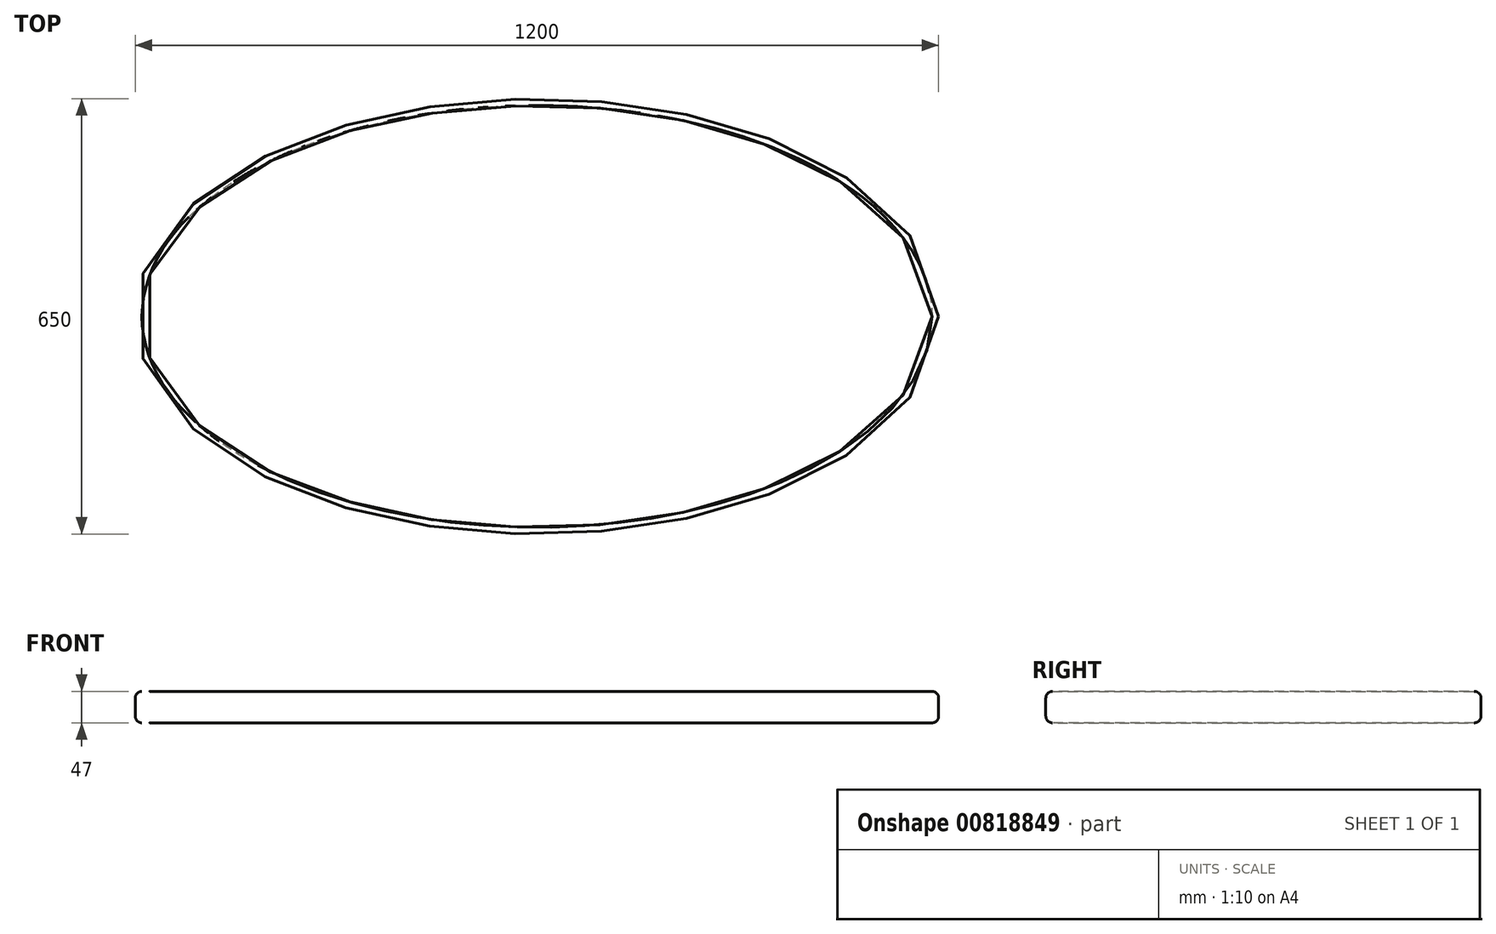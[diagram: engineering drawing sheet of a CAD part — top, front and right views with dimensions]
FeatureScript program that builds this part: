
annotation { "Feature Type Name" : "Feature", "Feature Type Description" : "" }
export const myFeature = defineFeature(function(context is Context, id is Id, definition is map)
    precondition{}
    {
        {
            var Q0;
            Q0=qCreatedBy(makeId("Top.planeOp"),FACE);
            var sketch = newSketch(context, id + "F0", { "sketchPlane" : qUnion([Q0])});
            skEllipse(sketch, "E0", {"center": v(0, 0) * mm, "majorRadius": 600 * mm, "minorRadius": 325 * mm, "majorAxis": v(1, 0)});
            skSolve(sketch);
        }
        {
            var Q0;
            Q0 = qSketchRegion(id + "F0", true);
            extrude(context, id + "F1", {"entities" : qUnion([Q0]), "depth" : 22 * mm, "offsetDistance" : 25 * mm});
        }
        {
            var Q0;
            Q0=makeQuery(id+"F1.opExtrude","CAP_FACE",FACE,{"disambiguationData":[OSD([sQuery(id+"F0.wireOp",EDGE,"E0")])],"isStart":true});
            var sketch = newSketch(context, id + "F2", { "sketchPlane" : qUnion([Q0])});
            skEllipse(sketch, "E1.0", {"center": v(0, 0) * mm, "majorRadius": 600 * mm, "minorRadius": 325 * mm, "majorAxis": v(1, 0)});
            skFitSpline(sketch, "E2.0", {"points": [v(577.9, -7.07) * mm, v(578.05, 0) * mm, v(577.9, 7.07) * mm, v(577.4, 14.11) * mm, v(576.6, 21.14) * mm, v(575.1, 30.5) * mm, v(572.43, 42.15) * mm, v(566.44, 60.74) * mm, v(555.74, 83.82) * mm, v(537.72, 111.12) * mm, v(518.37, 133.32) * mm, v(500.33, 150.6) * mm, v(485.53, 163.29) * mm, v(469.48, 175.66) * mm, v(455.07, 185.68) * mm, v(442.94, 193.5) * mm, v(433.54, 199.27) * mm, v(425.45, 203.99) * mm, v(418.83, 207.7) * mm, v(413.8, 210.47) * mm, v(408.7, 213.2) * mm, v(401.8, 216.8) * mm, v(393.06, 221.2) * mm, v(382.32, 226.33) * mm, v(367.72, 232.98) * mm, v(348.91, 240.9) * mm, v(325.53, 249.8) * mm, v(301.4, 258.07) * mm, v(268.25, 268.23) * mm, v(225.17, 279.26) * mm, v(180.22, 287.98) * mm, v(143.35, 293.52) * mm, v(115.3, 296.95) * mm, v(86.88, 299.64) * mm, v(62.95, 301.25) * mm, v(43.68, 302.15) * mm, v(29.17, 302.64) * mm, v(17.04, 302.89) * mm, v(7.3, 302.98) * mm, v(0, 303) * mm, v(-7.3, 302.98) * mm, v(-17.04, 302.89) * mm, v(-29.17, 302.64) * mm, v(-43.68, 302.15) * mm, v(-62.95, 301.25) * mm, v(-86.88, 299.64) * mm, v(-115.3, 296.95) * mm, v(-143.35, 293.52) * mm, v(-180.22, 287.98) * mm, v(-225.17, 279.26) * mm, v(-268.25, 268.23) * mm, v(-301.4, 258.07) * mm, v(-325.53, 249.8) * mm, v(-348.91, 240.9) * mm, v(-367.72, 232.98) * mm, v(-382.32, 226.33) * mm, v(-393.06, 221.2) * mm, v(-401.8, 216.8) * mm, v(-408.7, 213.2) * mm, v(-413.8, 210.47) * mm, v(-418.83, 207.7) * mm, v(-425.45, 203.99) * mm, v(-433.54, 199.27) * mm, v(-442.94, 193.5) * mm, v(-455.07, 185.68) * mm, v(-469.48, 175.66) * mm, v(-485.53, 163.29) * mm, v(-500.33, 150.6) * mm, v(-518.37, 133.32) * mm, v(-537.72, 111.12) * mm, v(-555.74, 83.82) * mm, v(-566.44, 60.74) * mm, v(-572.43, 42.15) * mm, v(-575.1, 30.5) * mm, v(-576.6, 21.14) * mm, v(-577.4, 14.11) * mm, v(-577.9, 7.07) * mm, v(-578.05, 0) * mm, v(-577.9, -7.07) * mm, v(-577.4, -14.11) * mm, v(-576.6, -21.14) * mm, v(-575.1, -30.5) * mm, v(-572.43, -42.15) * mm, v(-566.44, -60.74) * mm, v(-555.74, -83.82) * mm, v(-537.72, -111.12) * mm, v(-518.37, -133.32) * mm, v(-500.33, -150.6) * mm, v(-485.53, -163.29) * mm, v(-469.48, -175.66) * mm, v(-455.07, -185.68) * mm, v(-442.94, -193.5) * mm, v(-433.54, -199.27) * mm, v(-425.45, -203.99) * mm, v(-418.83, -207.7) * mm, v(-413.8, -210.47) * mm, v(-408.7, -213.2) * mm, v(-401.8, -216.8) * mm, v(-393.06, -221.2) * mm, v(-382.32, -226.33) * mm, v(-367.72, -232.98) * mm, v(-348.91, -240.9) * mm, v(-325.53, -249.8) * mm, v(-301.4, -258.07) * mm, v(-268.25, -268.23) * mm, v(-225.17, -279.26) * mm, v(-180.22, -287.98) * mm, v(-143.35, -293.52) * mm, v(-115.3, -296.95) * mm, v(-86.88, -299.64) * mm, v(-62.95, -301.25) * mm, v(-43.68, -302.15) * mm, v(-29.17, -302.64) * mm, v(-17.04, -302.89) * mm, v(-7.3, -302.98) * mm, v(0, -303) * mm, v(7.3, -302.98) * mm, v(17.04, -302.89) * mm, v(29.17, -302.64) * mm, v(43.68, -302.15) * mm, v(62.95, -301.25) * mm, v(86.88, -299.64) * mm, v(115.3, -296.95) * mm, v(143.35, -293.52) * mm, v(180.22, -287.98) * mm, v(225.17, -279.26) * mm, v(268.25, -268.23) * mm, v(301.4, -258.07) * mm, v(325.53, -249.8) * mm, v(348.91, -240.9) * mm, v(367.72, -232.98) * mm, v(382.32, -226.33) * mm, v(393.06, -221.2) * mm, v(401.8, -216.8) * mm, v(408.7, -213.2) * mm, v(413.8, -210.47) * mm, v(418.83, -207.7) * mm, v(425.45, -203.99) * mm, v(433.54, -199.27) * mm, v(442.94, -193.5) * mm, v(455.07, -185.68) * mm, v(469.48, -175.66) * mm, v(485.53, -163.29) * mm, v(500.33, -150.6) * mm, v(518.37, -133.32) * mm, v(537.72, -111.12) * mm, v(555.74, -83.82) * mm, v(566.44, -60.74) * mm, v(572.43, -42.15) * mm, v(575.1, -30.5) * mm, v(576.6, -21.14) * mm, v(577.4, -14.11) * mm, v(577.9, -7.07) * mm, v(578.05, 0) * mm, v(577.9, 7.07) * mm, v(577.9, -7.07) * mm]});
            skSolve(sketch);
        }
        {
            var Q0;
            Q0 = qSketchRegion(id + "F2", true);
            extrude(context, id + "F3", {"entities" : qUnion([Q0]), "operationType" : NewBodyOperationType.ADD, "depth" : 25 * mm, "offsetDistance" : 25 * mm});
        }
        {
            var Q0;
            Q0=makeQuery(id+"F3.boolean.opBoolean","MERGE",FACE,{"derivedFrom":[makeQuery(id+"F1.opExtrude","SWEPT_FACE",FACE,{"disambiguationData":[OSD([sQuery(id+"F0.wireOp",EDGE,"E0")])]}),makeQuery(id+"F3.opExtrude","SWEPT_FACE",FACE,{"disambiguationData":[OSD([sQuery(id+"F2.wireOp",EDGE,"E1.0")])]})]});
            fillet(context, id + "F4", {"entities" : qUnion([Q0]), "radius" : 10 * mm, "tangentPropagation" : true, "allowEdgeOverflow" : false});
        }
        {
            var Q0;
            Q0=makeQuery(id+"F0.imprint","IMPRINT",FACE,{"disambiguationData":[TD([[makeQuery(id+"F0.imprint","IMPRINT",EDGE,{"derivedFrom":sQuery(id+"F0.wireOp",EDGE,"E0")}),1.0]])]});
            var sketch = newSketch(context, id + "F5", { "sketchPlane" : qUnion([Q0])});
            skLineSegment(sketch, "E3", {"start": v(0, 0) * mm, "end": v(-445.69, 0) * mm, "construction": true});
            skLineSegment(sketch, "E4", {"start": v(0, 0) * mm, "end": v(-327.87, -152.89) * mm, "construction": true});
            skLineSegment(sketch, "E5", {"start": v(-416.58, -169.43) * mm, "end": v(-397.56, -210.21) * mm});
            skLineSegment(sketch, "E6", {"start": v(-397.56, -210.21) * mm, "end": v(-261.62, -146.82) * mm});
            skLineSegment(sketch, "E7", {"start": v(-261.62, -146.82) * mm, "end": v(-280.64, -106.04) * mm});
            skLineSegment(sketch, "E8", {"start": v(-280.64, -106.04) * mm, "end": v(-416.58, -169.43) * mm});
            skSolve(sketch);
        }
        {
            var Q0;
            Q0 = qSketchRegion(id + "F5", true);
            extrude(context, id + "F6", {"entities" : qUnion([Q0]), "operationType" : NewBodyOperationType.ADD, "oppositeDirection" : true, "depth" : 1 * mm, "offsetDistance" : 25 * mm});
        }
    });
